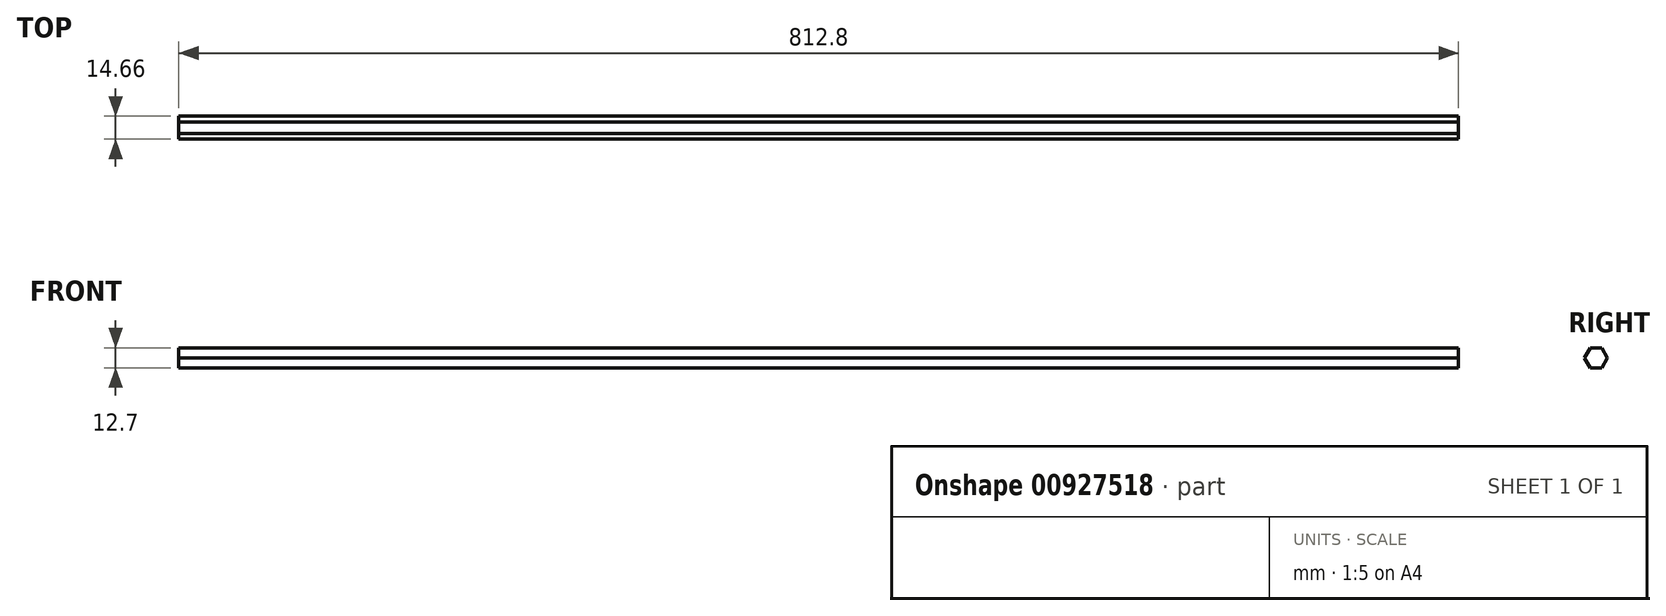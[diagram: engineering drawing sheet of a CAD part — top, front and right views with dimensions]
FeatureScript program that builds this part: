
annotation { "Feature Type Name" : "Feature", "Feature Type Description" : "" }
export const myFeature = defineFeature(function(context is Context, id is Id, definition is map)
    precondition{}
    {
        {
            var Q0;
            Q0=qCreatedBy(makeId("Right.planeOp"),FACE);
            var sketch = newSketch(context, id + "F0", { "sketchPlane" : qUnion([Q0])});
            skCircle(sketch, "E0.cCircle", {"center": v(0, 0) * mm, "radius": 6.35 * mm, "construction": true});
            skLineSegment(sketch, "E0.0", {"start": v(-3.67, 6.35) * mm, "end": v(3.67, 6.35) * mm});
            skLineSegment(sketch, "E0.1", {"start": v(3.67, 6.35) * mm, "end": v(7.33, 0) * mm});
            skLineSegment(sketch, "E0.2", {"start": v(7.33, 0) * mm, "end": v(3.67, -6.35) * mm});
            skLineSegment(sketch, "E0.3", {"start": v(3.67, -6.35) * mm, "end": v(-3.67, -6.35) * mm});
            skLineSegment(sketch, "E0.4", {"start": v(-3.67, -6.35) * mm, "end": v(-7.33, 0) * mm});
            skLineSegment(sketch, "E0.5", {"start": v(-7.33, 0) * mm, "end": v(-3.67, 6.35) * mm});
            skPoint(sketch, "E0.0.midPoint", {"position": v(0, 6.35) * mm});
            skSolve(sketch);
        }
        {
            var Q0;
            Q0=makeQuery(id+"F0.imprint","IMPRINT",FACE,{"disambiguationData":[TD([[makeQuery(id+"F0.imprint","IMPRINT",EDGE,{"derivedFrom":sQuery(id+"F0.wireOp",EDGE,"E0.0")}),-1.0]])]});
            extrude(context, id + "F1", {"entities" : qUnion([Q0]), "depth" : 812.8 * mm, "offsetDistance" : 25.4 * mm});
        }
    });
